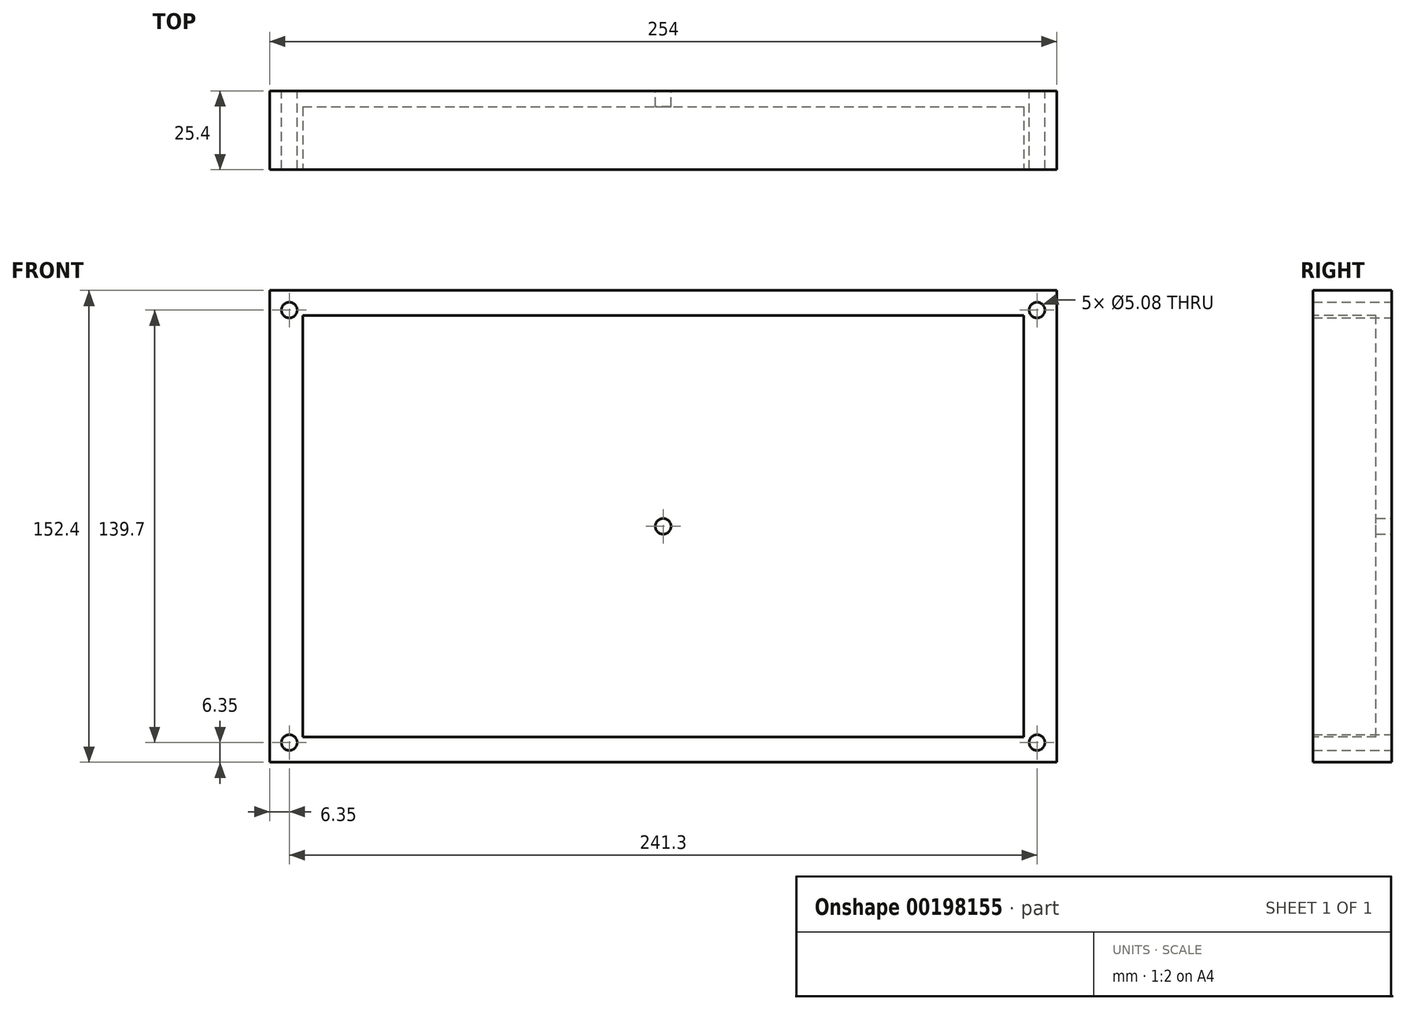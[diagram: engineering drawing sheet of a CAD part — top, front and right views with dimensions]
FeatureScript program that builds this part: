
annotation { "Feature Type Name" : "Feature", "Feature Type Description" : "" }
export const myFeature = defineFeature(function(context is Context, id is Id, definition is map)
    precondition{}
    {
        {
            var Q0;
            Q0=qCreatedBy(makeId("Front.planeOp"),FACE);
            var sketch = newSketch(context, id + "F0", { "sketchPlane" : qUnion([Q0])});
            skLineSegment(sketch, "E0.bottom", {"start": v(127, -76.2) * mm, "end": v(-127, -76.2) * mm});
            skLineSegment(sketch, "E0.top", {"start": v(127, 76.2) * mm, "end": v(-127, 76.2) * mm});
            skLineSegment(sketch, "E0.left", {"start": v(127, -76.2) * mm, "end": v(127, 76.2) * mm});
            skLineSegment(sketch, "E0.right", {"start": v(-127, -76.2) * mm, "end": v(-127, 76.2) * mm});
            skPoint(sketch, "E0.middle", {"position": v(0, 0) * mm});
            skLineSegment(sketch, "E1", {"start": v(0, -76.2) * mm, "end": v(0, -2.54) * mm});
            skLineSegment(sketch, "E2", {"start": v(-127, 0) * mm, "end": v(-2.54, 0) * mm});
            skLineSegment(sketch, "E3", {"start": v(-127, 76.2) * mm, "end": v(-127, 69.85) * mm});
            skLineSegment(sketch, "E4", {"start": v(-127, 76.2) * mm, "end": v(-120.65, 76.2) * mm});
            skLineSegment(sketch, "E5", {"start": v(-120.65, 76.2) * mm, "end": v(-120.65, 72.39) * mm});
            skLineSegment(sketch, "E6", {"start": v(-123.2, 69.85) * mm, "end": v(-127, 69.85) * mm});
            skCircle(sketch, "E7", {"center": v(-120.65, 69.85) * mm, "radius": 2.54 * mm});
            skCircle(sketch, "E8.MirrorC", {"center": v(120.65, 69.85) * mm, "radius": 2.54 * mm});
            skCircle(sketch, "E9.MirrorC", {"center": v(-120.65, -69.85) * mm, "radius": 2.54 * mm});
            skCircle(sketch, "E10.MirrorC", {"center": v(120.65, -69.85) * mm, "radius": 2.54 * mm});
            skCircle(sketch, "E11", {"center": v(0, 0) * mm, "radius": 2.54 * mm});
            skLineSegment(sketch, "E12.trimOffspring", {"start": v(0, 2.54) * mm, "end": v(0, 76.2) * mm});
            skLineSegment(sketch, "E13.trimOffspring", {"start": v(2.54, 0) * mm, "end": v(127, 0) * mm});
            skSolve(sketch);
        }
        {
            var Q0;
            Q0 = qSketchRegion(id + "F0", true);
            extrude(context, id + "F1", {"entities" : qUnion([Q0]), "depth" : 25.4 * mm});
        }
        {
            var Q0;
            Q0=makeQuery(id+"F1.opExtrude","CAP_FACE",FACE,{"disambiguationData":[OSD([sQuery(id+"F0.wireOp",EDGE,"E0.bottom"),sQuery(id+"F0.wireOp",EDGE,"E0.top"),sQuery(id+"F0.wireOp",EDGE,"E0.left"),sQuery(id+"F0.wireOp",EDGE,"E0.right"),sQuery(id+"F0.wireOp",EDGE,"E3"),sQuery(id+"F0.wireOp",EDGE,"E4"),sQuery(id+"F0.wireOp",EDGE,"E7"),sQuery(id+"F0.wireOp",EDGE,"E8.MirrorC"),sQuery(id+"F0.wireOp",EDGE,"E9.MirrorC"),sQuery(id+"F0.wireOp",EDGE,"E10.MirrorC")])],"isStart":false});
            var sketch = newSketch(context, id + "F2", { "sketchPlane" : qUnion([Q0])});
            skLineSegment(sketch, "E14.bottom", {"start": v(-116.34, -68.09) * mm, "end": v(116.34, -68.09) * mm});
            skLineSegment(sketch, "E14.top", {"start": v(-116.34, 68.09) * mm, "end": v(116.34, 68.09) * mm});
            skLineSegment(sketch, "E14.left", {"start": v(-116.34, -68.09) * mm, "end": v(-116.34, 68.09) * mm});
            skLineSegment(sketch, "E14.right", {"start": v(116.34, -68.09) * mm, "end": v(116.34, 68.09) * mm});
            skPoint(sketch, "E14.middle", {"position": v(0, 0) * mm});
            skSolve(sketch);
        }
        {
            var Q0;
            Q0 = qSketchRegion(id + "F2", true);
            extrude(context, id + "F3", {"entities" : qUnion([Q0]), "operationType" : NewBodyOperationType.REMOVE, "oppositeDirection" : true, "depth" : 20.32 * mm});
        }
    });
